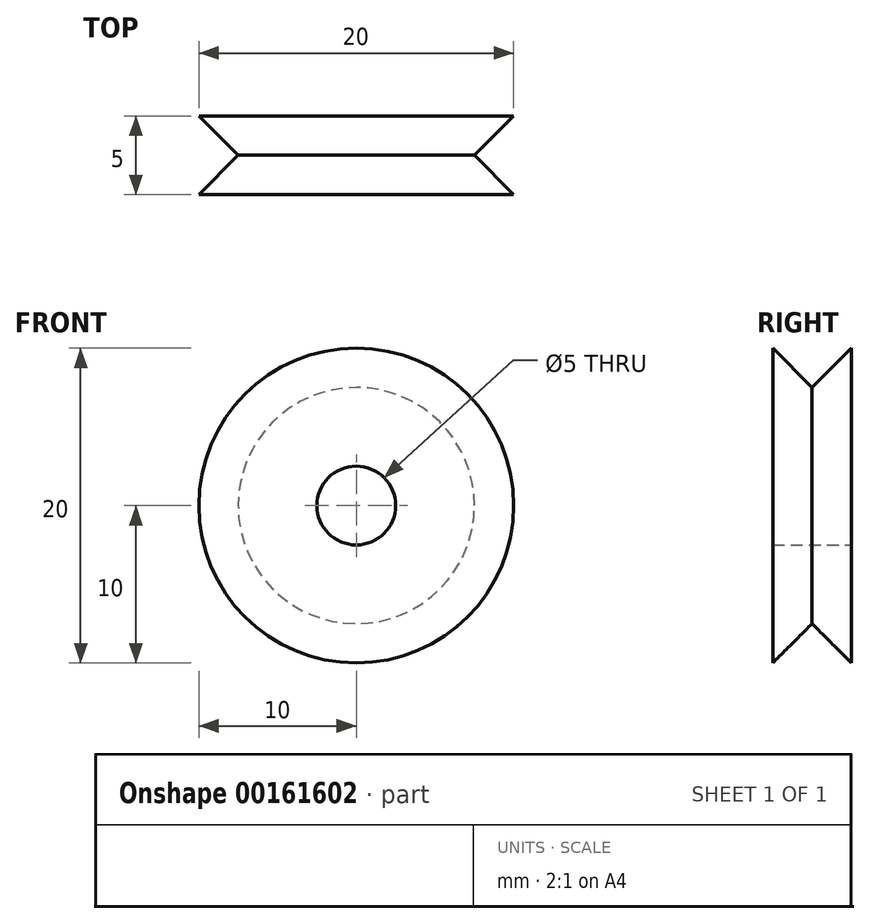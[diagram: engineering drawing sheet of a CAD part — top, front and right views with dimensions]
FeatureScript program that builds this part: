
annotation { "Feature Type Name" : "Feature", "Feature Type Description" : "" }
export const myFeature = defineFeature(function(context is Context, id is Id, definition is map)
    precondition{}
    {
        {
            var Q0;
            Q0=qCreatedBy(makeId("Front.planeOp"),FACE);
            var sketch = newSketch(context, id + "F0", { "sketchPlane" : qUnion([Q0])});
            skCircle(sketch, "E0", {"center": v(0, 0) * mm, "radius": 10 * mm});
            skCircle(sketch, "E1", {"center": v(0, 0) * mm, "radius": 2.5 * mm});
            skSolve(sketch);
        }
        {
            var Q0;
            Q0 = qSketchRegion(id + "F0", true);
            extrude(context, id + "F1", {"entities" : qUnion([Q0]), "depth" : 2.5 * mm});
        }
        {
            var Q0;
            Q0=makeQuery(id+"F1.opExtrude","CAP_EDGE",EDGE,{"disambiguationData":[OSD([sQuery(id+"F0.wireOp",EDGE,"E0")])],"isStart":true});
            chamfer(context, id + "F2", {"entities" : qUnion([Q0]), "width" : 2.5 * mm, "tangentPropagation" : true});
        }
        {
            var Q0;
            Q0=makeQuery(id+"F1.opExtrude","SWEPT_BODY",BODY,{"disambiguationData":[OSD([sQuery(id+"F0.wireOp",EDGE,"E0")])]});
            var Q1;
            Q1=qCreatedBy(makeId("Front.planeOp"),FACE);
            mirror(context, id + "F3", {"operationType" : NewBodyOperationType.ADD, "entities" : qUnion([Q0]), "mirrorPlane" : qUnion([Q1])});
        }
    });
